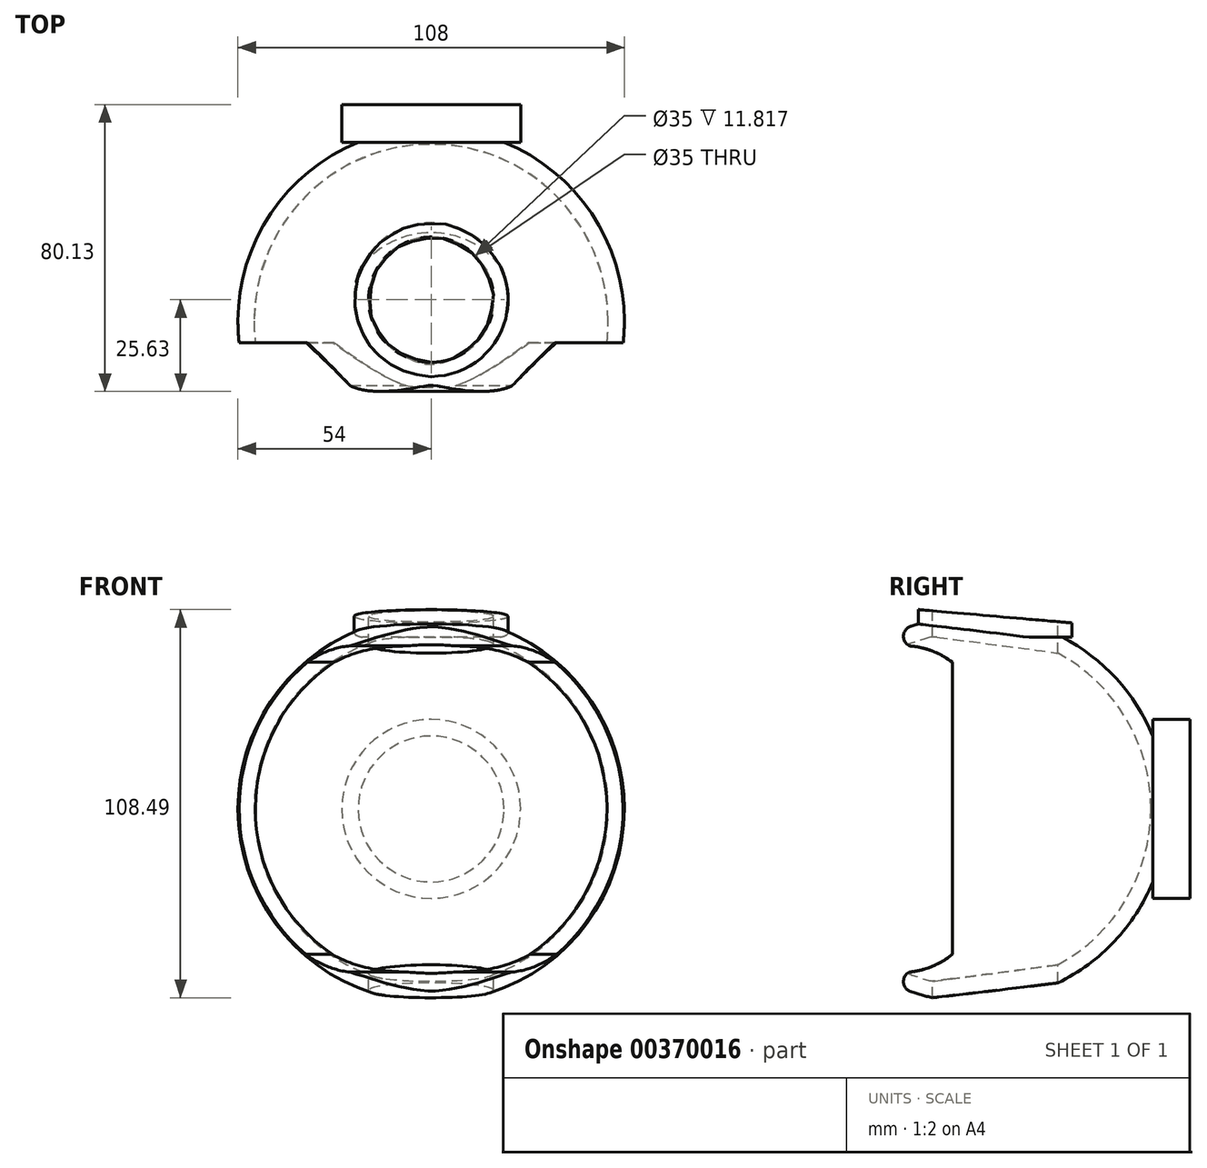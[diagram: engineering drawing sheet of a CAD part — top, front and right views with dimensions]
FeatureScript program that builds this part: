
annotation { "Feature Type Name" : "Feature", "Feature Type Description" : "" }
export const myFeature = defineFeature(function(context is Context, id is Id, definition is map)
    precondition{}
    {
        {
            var Q0;
            Q0=qCreatedBy(makeId("Front.planeOp"),FACE);
            var sketch = newSketch(context, id + "F0", { "sketchPlane" : qUnion([Q0])});
            skArc(sketch, "E0", {"start": v(54, 0) * mm, "mid": v(0, 54) * mm, "end": v(-54, 0) * mm});
            skArc(sketch, "E1", {"start": v(49.5, 0) * mm, "mid": v(0, 49.5) * mm, "end": v(-49.5, 0) * mm});
            skLineSegment(sketch, "E2", {"start": v(-54, 0) * mm, "end": v(-49.5, 0) * mm});
            skLineSegment(sketch, "E3", {"start": v(54, 0) * mm, "end": v(49.5, 0) * mm});
            skSolve(sketch);
        }
        {
            var Q0;
            Q0=qSketchRegion(id+"F0",true);
            var Q1;
            Q1=sQuery(id+"F0.wireOp",EDGE,"E2");
            revolve(context, id + "F1", {"entities" : qUnion([Q0]), "axis" : qUnion([Q1]), "revolveType" : RevolveType.FULL});
        }
        {
            var Q0;
            Q0=qCreatedBy(makeId("Right.planeOp"),FACE);
            cPlane(context, id + "F2", {"entities" : qUnion([Q0]), "cplaneType" : CPlaneType.OFFSET, "offset" : 54 * mm, "width" : 150 * mm, "height" : 150 * mm});
        }
        {
            var Q0;
            Q0=qCreatedBy(id+"F2.planeOp",FACE);
            var sketch = newSketch(context, id + "F3", { "sketchPlane" : qUnion([Q0])});
            skCircle(sketch, "E4", {"center": v(0, 0) * mm, "radius": 54 * mm});
            skCircle(sketch, "E5", {"center": v(0, 0) * mm, "radius": 49 * mm});
            skPoint(sketch, "E6", {"position": v(54, 0) * mm});
            skLineSegment(sketch, "E7", {"start": v(54, 0) * mm, "end": v(54, 65) * mm, "construction": true});
            skLineSegment(sketch, "E8", {"start": v(54, 0) * mm, "end": v(54, -65) * mm, "construction": true});
            skPoint(sketch, "E9", {"position": v(0, 54) * mm});
            skPoint(sketch, "E10", {"position": v(-18, 54) * mm});
            skPoint(sketch, "E11", {"position": v(0, 49) * mm});
            skPoint(sketch, "E12", {"position": v(-6, 49) * mm});
            skLineSegment(sketch, "E13", {"start": v(-18, 54) * mm, "end": v(-18, -50.91) * mm, "construction": true});
            skLineSegment(sketch, "E14", {"start": v(-18, 50.91) * mm, "end": v(-18, 45.57) * mm});
            skLineSegment(sketch, "E15", {"start": v(-18, -50.91) * mm, "end": v(-18, -45.57) * mm});
            skPoint(sketch, "E16", {"position": v(-6, 41) * mm});
            skPoint(sketch, "E17", {"position": v(-6, -48.63) * mm});
            skPoint(sketch, "E18", {"position": v(-6, -40.63) * mm});
            skLineSegment(sketch, "E19", {"start": v(-6, 41) * mm, "end": v(-6, -40.63) * mm});
            skArc(sketch, "E20", {"start": v(-18, -45.57) * mm, "mid": v(-11.63, -44) * mm, "end": v(-6, -40.63) * mm});
            skArc(sketch, "E21", {"start": v(-6, 41) * mm, "mid": v(-11.66, 44.18) * mm, "end": v(-18, 45.57) * mm});
            skArc(sketch, "E22", {"start": v(-18, 50.91) * mm, "mid": v(-19.63, 48.24) * mm, "end": v(-18, 45.57) * mm});
            skArc(sketch, "E23", {"start": v(-18, -45.57) * mm, "mid": v(-19.63, -48.24) * mm, "end": v(-18, -50.91) * mm});
            skSolve(sketch);
        }
        {
            var Q0;
            Q0=makeQuery(id+"F3.imprint","IMPRINT",FACE,{"disambiguationData":[TD([[makeQuery(id+"F3.imprint","IMPRINT",EDGE,{"derivedFrom":sQuery(id+"F3.wireOp",EDGE,"E19")}),-1.0]])]});
            var Q1;
            {var subQ0=sQuery(id+"F3.wireOp",EDGE,"E22");Q1=makeQuery(id+"F3.imprint","IMPRINT",FACE,{"disambiguationData":[TD([[makeQuery(id+"F3.imprint","IMPRINT",EDGE,{"derivedFrom":subQ0}),-1.0]])]});}
            extrude(context, id + "F4", {"entities" : qUnion([Q0, Q1]), "operationType" : NewBodyOperationType.REMOVE, "oppositeDirection" : true, "depth" : 108 * mm});
        }
        {
            var Q0;
            Q0=qCreatedBy(makeId("Top.planeOp"),FACE);
            cPlane(context, id + "F5", {"entities" : qUnion([Q0]), "cplaneType" : CPlaneType.OFFSET, "offset" : 54 * mm, "width" : 150 * mm, "height" : 150 * mm});
        }
        {
            var Q0;
            Q0=qCreatedBy(id+"F5.planeOp",FACE);
            var sketch = newSketch(context, id + "F6", { "sketchPlane" : qUnion([Q0])});
            skPoint(sketch, "E24", {"position": v(0, -18) * mm});
            skPoint(sketch, "E25", {"position": v(0, 6) * mm});
            skCircle(sketch, "E26", {"center": v(0, 6) * mm, "radius": 17.5 * mm});
            skSolve(sketch);
        }
        {
            var Q0;
            Q0=qSketchRegion(id+"F6",true);
            extrude(context, id + "F7", {"entities" : qUnion([Q0]), "operationType" : NewBodyOperationType.REMOVE, "oppositeDirection" : true, "depth" : 108 * mm});
        }
        {
            var Q0;
            Q0=qCreatedBy(makeId("Front.planeOp"),FACE);
            cPlane(context, id + "F8", {"entities" : qUnion([Q0]), "cplaneType" : CPlaneType.OFFSET, "offset" : 50 * mm, "oppositeDirection" : true, "width" : 150 * mm, "height" : 150 * mm});
        }
        {
            var Q0;
            Q0=qCreatedBy(id+"F8.planeOp",FACE);
            var sketch = newSketch(context, id + "F9", { "sketchPlane" : qUnion([Q0])});
            skCircle(sketch, "E27", {"center": v(0, 0) * mm, "radius": 25 * mm});
            skSolve(sketch);
        }
        {
            var Q0;
            Q0=qSketchRegion(id+"F9",true);
            extrude(context, id + "F10", {"entities" : qUnion([Q0]), "operationType" : NewBodyOperationType.ADD, "oppositeDirection" : true, "depth" : 10.5 * mm});
        }
        {
            var Q0;
            Q0=qCreatedBy(id+"F5.planeOp",FACE);
            cPlane(context, id + "F11", {"entities" : qUnion([Q0]), "cplaneType" : CPlaneType.OFFSET, "offset" : 4 * mm, "width" : 150 * mm, "height" : 150 * mm});
        }
        {
            var Q0;
            Q0=qCreatedBy(id+"F11.planeOp",FACE);
            var sketch = newSketch(context, id + "F12", { "sketchPlane" : qUnion([Q0])});
            skCircle(sketch, "E28.0", {"center": v(0, 6) * mm, "radius": 17.5 * mm});
            skCircle(sketch, "E29", {"center": v(0, 6) * mm, "radius": 21.5 * mm});
            skSolve(sketch);
        }
        {
            var Q0;
            Q0 = qSketchRegion(id + "F12", true);
            extrude(context, id + "F13", {"entities" : qUnion([Q0]), "operationType" : NewBodyOperationType.ADD, "oppositeDirection" : true, "depth" : 10 * mm});
        }
        {
            var Q0;
            Q0=qCreatedBy(makeId("Right.planeOp"),FACE);
            var sketch = newSketch(context, id + "F14", { "sketchPlane" : qUnion([Q0])});
            skFitSpline(sketch, "E30.0", {"points": [v(15.48, 48) * mm, v(14.66, 48.1) * mm, v(12.99, 48.31) * mm, v(10.81, 48.58) * mm, v(9.03, 48.8) * mm, v(7.21, 49.02) * mm, v(4.96, 49.3) * mm, v(2.72, 49.57) * mm, v(0.93, 49.78) * mm, v(-0.82, 50) * mm, v(-2.5, 50.2) * mm, v(-4.12, 50.4) * mm, v(-5.3, 50.53) * mm, v(-6.45, 50.67) * mm, v(-7.89, 50.84) * mm, v(-9.22, 51) * mm, v(-10.44, 51.14) * mm, v(-11.58, 51.27) * mm, v(-12.8, 51.41) * mm, v(-13.79, 51.53) * mm, v(-14.42, 51.6) * mm, v(-14.94, 51.66) * mm, v(-15.38, 51.71) * mm, v(-15.5, 51.73) * mm, v(-15.5, 51.73) * mm]});
            skPoint(sketch, "E31", {"position": v(-15.5, 55.73) * mm});
            skLineSegment(sketch, "E32.0", {"start": v(15.48, 48) * mm, "end": v(27.5, 48) * mm});
            skPoint(sketch, "E33", {"position": v(27.5, 52) * mm});
            skLineSegment(sketch, "E34", {"start": v(-15.5, 55.73) * mm, "end": v(27.5, 52) * mm});
            skLineSegment(sketch, "E35.0", {"start": v(-15.5, 58) * mm, "end": v(27.5, 58) * mm});
            skLineSegment(sketch, "E36", {"start": v(27.5, 58) * mm, "end": v(27.5, 52) * mm});
            skLineSegment(sketch, "E37", {"start": v(-15.5, 58) * mm, "end": v(-15.5, 55.73) * mm});
            skLineSegment(sketch, "E38", {"start": v(-15.5, 58) * mm, "end": v(-16.5, 58) * mm});
            skLineSegment(sketch, "E39", {"start": v(-16.5, 58) * mm, "end": v(-16.5, 55.72) * mm});
            skLineSegment(sketch, "E40", {"start": v(-16.5, 55.72) * mm, "end": v(-15.5, 55.73) * mm});
            skSolve(sketch);
        }
        {
            var Q0;
            Q0 = qSketchRegion(id + "F14", true);
            extrude(context, id + "F15", {"entities" : qUnion([Q0]), "operationType" : NewBodyOperationType.REMOVE, "endBound" : BoundingType.SYMMETRIC, "oppositeDirection" : true, "depth" : 45 * mm});
        }
    });
